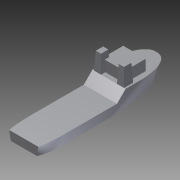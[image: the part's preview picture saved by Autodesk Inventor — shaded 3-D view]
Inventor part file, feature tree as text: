
AUTODESK INVENTOR PART (.ipt)
format: ipt  version: 2011 (Build 150239000, 239)  size: 178,688 bytes
history: native  units: mm
features: sketch x11, plane x8, extrude x3, mirror x3, loft x1
ambient origin geometry x8: Origin, YZ Plane, XZ Plane, XY Plane, X Axis, Y Axis, Z Axis, Center Point
bodies: Solid1 (feature_tree)
feature tree (26):
  sketch  "Sketch1"  dims[d0=1000.0mm d1=250.0mm]
  plane  "Work Plane1"
  sketch  "Sketch2"  dims[d2=-130.0mm d3=200.0mm]
  plane  "Work Plane2"
  sketch  "Sketch4"  dims[d4=400.0mm d5=0.0mm d6=90.0deg]
  plane  "Work Plane3"
  sketch  "Sketch5"  dims[d7=0.0mm d8=90.0deg d9=135.0deg]
  plane  "Work Plane4"
  sketch  "Sketch6"  dims[d10=10.0mm d11=0.0mm]
  plane  "Work Plane5"
  sketch  "Sketch7"  dims[d12=160.0mm]
  plane  "Work Plane6"
  sketch  "Sketch8"  dims[d13=85.0mm]
  plane  "Work Plane7"
  sketch  "Sketch9"  dims[d14=80.0mm d15=0.0mm]
  plane  "Work Plane8"
  loft  "Loft1"
  extrude  "Extrusion1"  Depth=200.0mm
  mirror  "Mirror1"
  extrude  "Extrusion2"  TaperAngle=0.0deg  [1 undecoded]
  mirror  "Mirror2"
  extrude  "Extrusion3"  TaperAngle=135.0deg  [1 undecoded]
  mirror  "Mirror3"
  sketch  "Sketch10"  dims[d16=130.0mm d17=-0.523599mm]
  sketch  "Sketch11"
  sketch  "Sketch12"
note: 2 required parameter values undecoded (feature->parameter linkage not recoverable at this tier; creation-order binding heuristic only, values carry confidence <= 0.55)
